# Revit family: IS_ConnectAir_E0180_BIM_DE
name_source: partatom
category: Plumbing Fixtures
revit_build: Autodesk Revit MEP 2014 (Build: 20130308_1515(x64)
units: mm (PartAtom-declared; Revit-internal decimal feet)

## types (2) — shared parameters
Accessories = www.idealstandard.de\ersatzteile
AreaUnits = millimeters
Assembly Code = C1030200
AssetType = Fixed
Brand = Ideal Standard
Category = Bidet
CodePerformance = DIN EN 14528 CL 25, DIN EN 35
ConnectionType = Plumbing
DurationUnit = year
ExpectedLife = 25
Features = Connect Air floor standing bidet
GrossWeight = 0
IfcExportAs = IfcSanitaryType
IfcExportType = BIDET
InstallationInstructions = www.idealstandard.de\produkte
LinearUnits = millimeters
ManufacturerURL = www.idealstandard.de
Material = Vitreous china
NBSDescription = Bidets
NBSReference = 45-35-70/320
NominalHeight = 400 mm
NominalLength = 549 mm
NominalWidth = 366 mm
ProductInformation = www.idealstandard.de\produkte
Shape = Sculptured
Size = 360x480x310mm
Space = Internal
URL = www.idealstandard.com
Uniclass2015Code = Pr_40_20_06_11
Uniclass2015Title = Bidets
Uniclass2015Version = Products v1.1
Version = 1
VolumeUnits = Litres
WarrantyDescription = Manufacturers Warranty
WarrantyDurationUnit = year
zero-valued in all types: CWFU, Cost, Default Elevation, DrainSize, HWFU, WFU

## per-type parameters (varying)
| type | BIMObjectName | BarCode | Color | Description | Finish | Model | ModelNumber | ModelReference | Name | NettWeight |
| E018001 - Connect Air floor standing bidet | ISI_IdealStandard_Bidets_ConnectAir_E018001 | 5017830514329 | white | E018001 Connect Air floor standing bidet | white | E018001 | E018001 | E018001 Connect Air floor standing bidet | Bidets_ConnectAir_E018001_IdealStandard | 20,5 kg |
| E0180MA - Connect Air floor standing bidet | ISI_IdealStandard_Bidets_ConnectAir_E0180MA | 5017830518303 | white with ideal plus | E0180MA Connect Air floor standing bidet | white with ideal plus | E0180MA | E0180MA | E0180MA Connect Air floor standing bidet | Bidets_ConnectAir_E0180MA_IdealStandard | 18,5 kg |

## geometry (parser evidence)
native form markers: Sweep x2
no freeform markers — native parametric forms only
